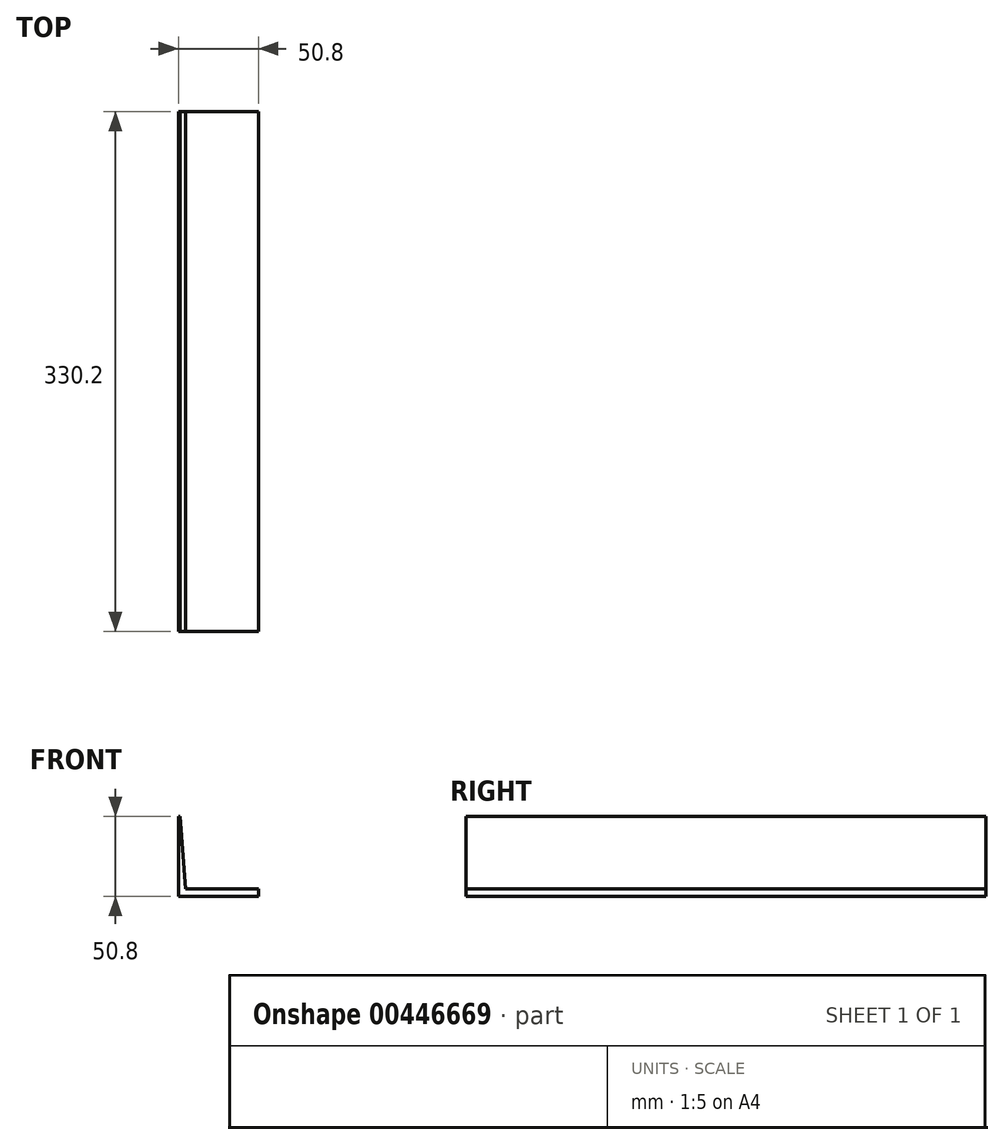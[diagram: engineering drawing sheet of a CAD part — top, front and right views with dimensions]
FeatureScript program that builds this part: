
annotation { "Feature Type Name" : "Feature", "Feature Type Description" : "" }
export const myFeature = defineFeature(function(context is Context, id is Id, definition is map)
    precondition{}
    {
        {
            var Q0;
            Q0=qCreatedBy(makeId("Front.planeOp"),FACE);
            var sketch = newSketch(context, id + "F0", { "sketchPlane" : qUnion([Q0])});
            skLineSegment(sketch, "E0", {"start": v(0, 0) * mm, "end": v(50.8, 0) * mm});
            skLineSegment(sketch, "E1", {"start": v(50.8, 0) * mm, "end": v(50.8, 4.75) * mm});
            skLineSegment(sketch, "E2", {"start": v(50.8, 4.75) * mm, "end": v(4.75, 4.75) * mm});
            skLineSegment(sketch, "E3", {"start": v(4.75, 4.75) * mm, "end": v(1.27, 50.8) * mm});
            skLineSegment(sketch, "E4", {"start": v(1.27, 50.8) * mm, "end": v(0, 50.8) * mm});
            skLineSegment(sketch, "E5", {"start": v(0, 50.8) * mm, "end": v(0, 0) * mm});
            skSolve(sketch);
        }
        {
            var Q0;
            Q0 = qSketchRegion(id + "F0", true);
            extrude(context, id + "F1", {"entities" : qUnion([Q0]), "depth" : 330.2 * mm, "offsetDistance" : 25.4 * mm});
        }
    });
